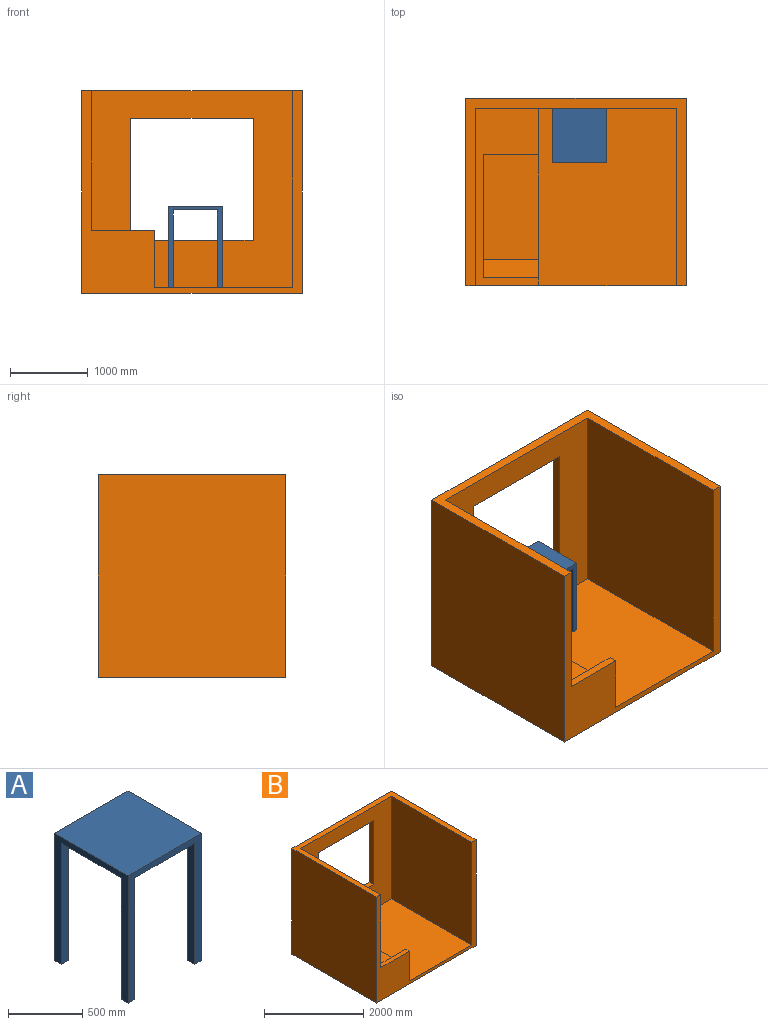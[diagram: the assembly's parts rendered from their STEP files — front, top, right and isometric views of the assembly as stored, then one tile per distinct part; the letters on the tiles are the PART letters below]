
ASSEMBLY  parts=2 mates=2
PART A: 18 faces, bbox 698.5x698.5x1050.9 mm
  f0: plane 1050.93x698.5mm, normal (-1,0,0), area 162499.7mm2, adj f1,f3,f4,f5,f10,f11,f13,f14
  f1: plane 1050.93x698.5mm, normal (0,-1,0), area 162499.7mm2, adj f0,f2,f4,f5,f7,f8,f9,f11
  f2: plane 1050.93x698.5mm, normal (1,0,0), area 162499.7mm2, adj f1,f3,f4,f5,f6,f8,f15,f17
  f3: plane 1050.93x698.5mm, normal (0,1,0), area 162499.7mm2, adj f0,f2,f4,f5,f12,f14,f16,f17
  f4: plane 698.5x698.5mm, normal (0,0,1), area 487902.2mm2, adj f0,f1,f2,f3
  f5: plane 698.5x698.5mm, normal (0,0,-1), area 471773.2mm2, adj f0,f1,f2,f3,f6,f7,f9,f10
  f6: plane 1000.13x63.5mm, normal (0,1,0), area 63507.9mm2, adj f2,f5,f7,f8
  f7: plane 1000.13x63.5mm, normal (-1,0,0), area 63507.9mm2, adj f1,f5,f6,f8
  f8: plane 63.5x63.5mm, normal (0,0,-1), area 4032.3mm2, adj f1,f2,f6,f7
  f9: plane 1000.13x63.5mm, normal (1,0,0), area 63507.9mm2, adj f1,f5,f10,f11
  f10: plane 1000.13x63.5mm, normal (0,1,0), area 63507.9mm2, adj f0,f5,f9,f11
  f11: plane 63.5x63.5mm, normal (0,0,-1), area 4032.3mm2, adj f0,f1,f9,f10
  f12: plane 1000.13x63.5mm, normal (1,0,0), area 63507.9mm2, adj f3,f5,f13,f14
  f13: plane 1000.13x63.5mm, normal (0,-1,0), area 63507.9mm2, adj f0,f5,f12,f14
  f14: plane 63.5x63.5mm, normal (0,0,-1), area 4032.3mm2, adj f0,f3,f12,f13
  f15: plane 1000.13x63.5mm, normal (0,-1,0), area 63507.9mm2, adj f2,f5,f16,f17
  f16: plane 1000.13x63.5mm, normal (-1,0,0), area 63507.9mm2, adj f3,f5,f15,f17
  f17: plane 63.5x63.5mm, normal (0,0,-1), area 4032.3mm2, adj f2,f3,f15,f16
PART B: 29 faces, bbox 2844.8x2413x2616.2 mm
  f0: plane 330.2x76.2mm, normal (-1,0,0), area 25161.2mm2, adj f2,f19,f24,f27
  f1: plane 304.8x127mm, normal (0,1,0), area 27096.7mm2, adj f3,f14,f15,f18,f23,f24
  f2: plane 711.2x406.4mm, normal (0,-1,0), area 79354.7mm2, adj f0,f3,f18,f19,f21,f24
  f3: plane 2286x812.8mm, normal (0,0,1), area 730422.3mm2, adj f1,f2,f4,f5,f10,f18,f20,f21
  f4: plane 2286x1803.4mm, normal (1,0,0), area 4122572.4mm2, adj f3,f5,f10,f11
  f5: plane 2590.8x2540mm, normal (0,-1,0), area 3540638.1mm2, adj f3,f4,f9,f11,f13,f14,f15,f16
  f6: plane 2616.2x2413mm, normal (1,0,0), area 6312890.6mm2, adj f7,f10,f11,f12
  f7: plane 2844.8x2616.2mm, normal (0,1,0), area 4962570.7mm2, adj f6,f8,f11,f12,f14,f15,f16,f17
  f8: plane 2616.2x2413mm, normal (-1,0,0), area 6312890.6mm2, adj f7,f10,f11,f12
  f9: plane 2540x2286mm, normal (-1,0,0), area 5806440mm2, adj f5,f10,f11,f13
  f10: plane 2844.8x2616.2mm, normal (0,-1,0), area 1460642.2mm2, adj f3,f4,f6,f8,f9,f11,f12,f13
  f11: plane 2844.8x2413mm, normal (0,0,1), area 941933.6mm2, adj f4,f5,f6,f7,f8,f9,f10
  f12: plane 2844.8x2413mm, normal (0,0,-1), area 6864502.4mm2, adj f6,f7,f8,f10
  f13: plane 2286x1778mm, normal (0,0,1), area 4064508mm2, adj f5,f9,f10,f18
  f14: plane 1574.8x127mm, normal (1,0,0), area 199999.6mm2, adj f1,f5,f7,f15,f17,f22
  f15: plane 1574.8x127mm, normal (0,0,1), area 199999.6mm2, adj f1,f5,f7,f14,f16,f22
  f16: plane 1574.8x127mm, normal (-1,0,0), area 199999.6mm2, adj f5,f7,f15,f17
  f17: plane 1574.8x127mm, normal (0,0,-1), area 199999.6mm2, adj f5,f7,f14,f16
  f18: plane 2286x736.6mm, normal (1,0,0), area 928420.7mm2, adj f1,f2,f3,f5,f10,f13,f19,f20
  f19: plane 1949.77x711.2mm, normal (0,0,1), area 1341039.9mm2, adj f0,f2,f18,f20,f21,f22,f23,f25
  f20: plane 711.2x406.4mm, normal (0,0.87,0.5), area 333745mm2, adj f3,f18,f19,f21
  f21: plane 2184.4x406.4mm, normal (1,0,0), area 794429.4mm2, adj f2,f3,f19,f20,f22,f24
  f22: plane 635x330.2mm, normal (0,-1,0), area 198064.1mm2, adj f14,f15,f19,f21,f23,f24
  f23: plane 330.2x76.2mm, normal (-1,0,0), area 25161.2mm2, adj f1,f19,f22,f24,f28
  f24: plane 711.2x598.86mm, normal (0,0,-1), area 414293.9mm2, adj f0,f1,f2,f18,f21,f22,f23,f27
  f25: plane 446.46x25.4mm, normal (1,0,0), area 11340mm2, adj f19,f26,f27,f28
  f26: plane 446.46x76.2mm, normal (0,0,1), area 34020mm2, adj f18,f25,f27,f28
  f27: plane 355.6x76.2mm, normal (0,1,0), area 27096.7mm2, adj f0,f18,f24,f25,f26
  f28: plane 355.6x76.2mm, normal (0,-1,0), area 27096.7mm2, adj f18,f23,f24,f25,f26
PLACE A t=(-1703.21,-688.99,1303.51)mm
PLACE B t=(-1601.7,-1060.52,303.38)mm
MATE planar A.f8 <-> B.f13  axis (0,0,-1) through (-1392.97,-941.91,303.38)mm
MATE parallel A.f3 <-> B.f5  axis (0,1,0) through (-1996.22,-275.16,303.38)mm
